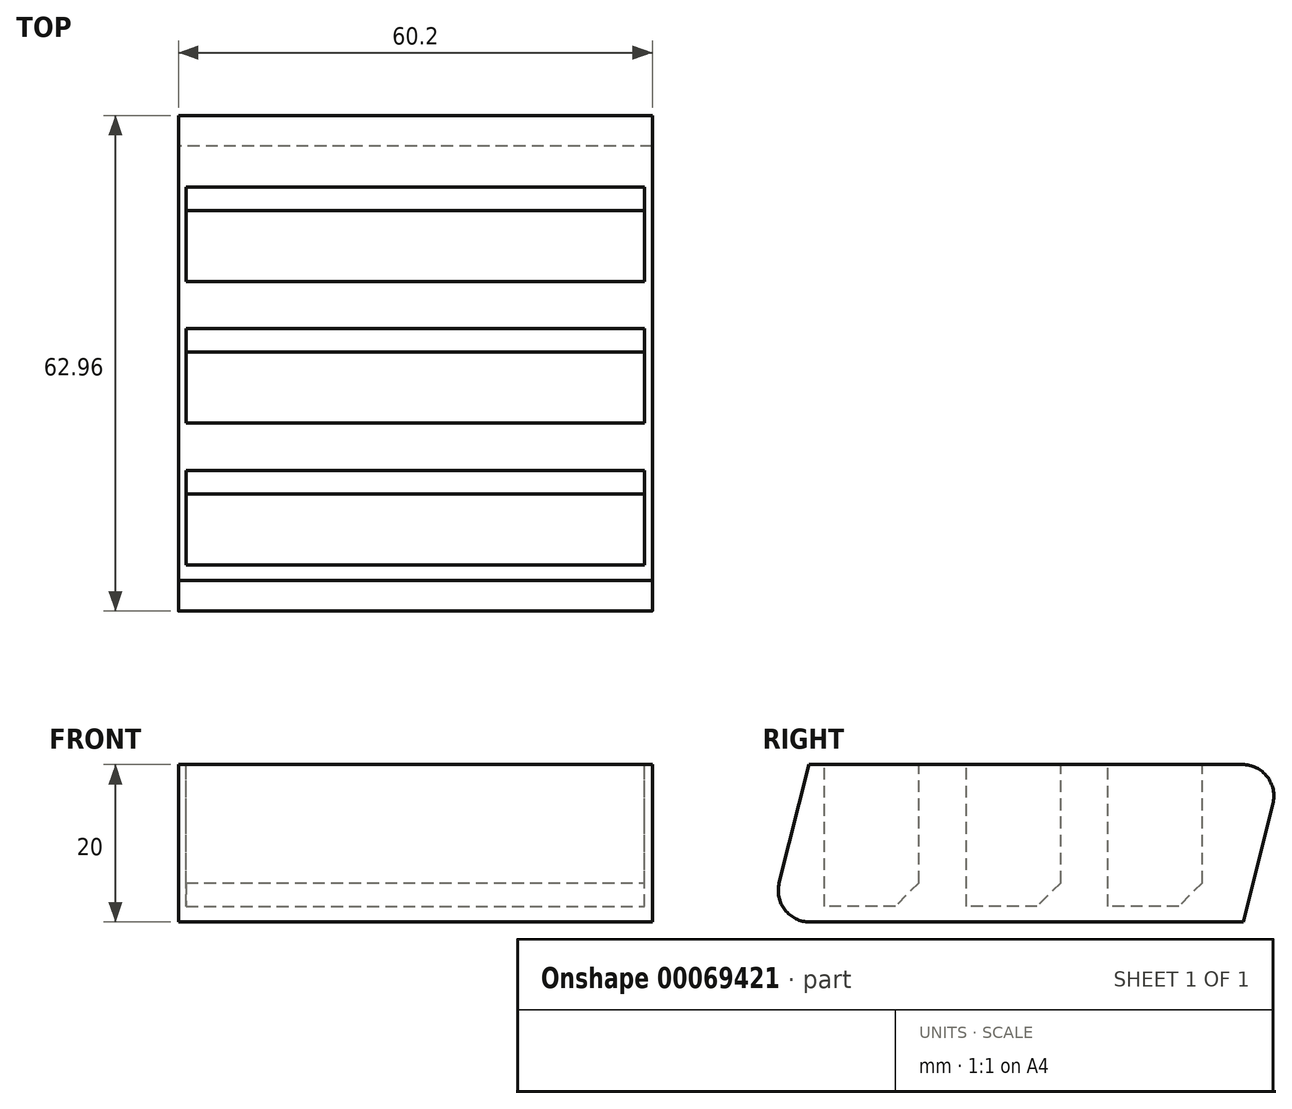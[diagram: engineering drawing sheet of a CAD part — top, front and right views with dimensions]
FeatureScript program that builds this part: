
annotation { "Feature Type Name" : "Feature", "Feature Type Description" : "" }
export const myFeature = defineFeature(function(context is Context, id is Id, definition is map)
    precondition{}
    {
        {
            var Q0;
            Q0=qCreatedBy(makeId("Top.planeOp"),FACE);
            var sketch = newSketch(context, id + "F0", { "sketchPlane" : qUnion([Q0])});
            skLineSegment(sketch, "E0.rect.bottom", {"start": v(30.1, -30.1) * mm, "end": v(-30.1, -30.1) * mm});
            skLineSegment(sketch, "E0.rect.top", {"start": v(30.1, 30.1) * mm, "end": v(-30.1, 30.1) * mm});
            skLineSegment(sketch, "E0.rect.left", {"start": v(30.1, -30.1) * mm, "end": v(30.1, 30.1) * mm});
            skLineSegment(sketch, "E0.rect.right", {"start": v(-30.1, -30.1) * mm, "end": v(-30.1, 30.1) * mm});
            skPoint(sketch, "E0.rect.middle", {"position": v(0, 0) * mm});
            skSolve(sketch);
        }
        {
            var Q0;
            Q0=makeQuery(id+"F0.imprint","IMPRINT",FACE,{"disambiguationData":[TD([[makeQuery(id+"F0.imprint","IMPRINT",EDGE,{"derivedFrom":sQuery(id+"F0.wireOp",EDGE,"E0.rect.bottom")}),-1.0]])]});
            cPlane(context, id + "F1", {"entities" : qUnion([Q0]), "cplaneType" : CPlaneType.OFFSET, "offset" : 20 * mm, "width" : 150 * mm, "height" : 150 * mm});
        }
        {
            var Q0;
            Q0=qCreatedBy(id+"F1.planeOp",FACE);
            var sketch = newSketch(context, id + "F2", { "sketchPlane" : qUnion([Q0])});
            skLineSegment(sketch, "E1.0.0", {"start": v(-30.1, -30.1) * mm, "end": v(30.1, -30.1) * mm, "construction": true});
            skLineSegment(sketch, "E1.0.1", {"start": v(30.1, -30.1) * mm, "end": v(30.1, 30.1) * mm, "construction": true});
            skLineSegment(sketch, "E1.0.2", {"start": v(30.1, 30.1) * mm, "end": v(-30.1, 30.1) * mm, "construction": true});
            skLineSegment(sketch, "E1.0.3", {"start": v(-30.1, 30.1) * mm, "end": v(-30.1, -30.1) * mm, "construction": true});
            skLineSegment(sketch, "E2", {"start": v(0, 0) * mm, "end": v(0, 5) * mm, "construction": true});
            skLineSegment(sketch, "E3.rect.bottom", {"start": v(30.1, 35.1) * mm, "end": v(-30.1, 35.1) * mm});
            skLineSegment(sketch, "E3.rect.top", {"start": v(30.1, -25.1) * mm, "end": v(-30.1, -25.1) * mm});
            skLineSegment(sketch, "E3.rect.left", {"start": v(30.1, 35.1) * mm, "end": v(30.1, -25.1) * mm});
            skLineSegment(sketch, "E3.rect.right", {"start": v(-30.1, 35.1) * mm, "end": v(-30.1, -25.1) * mm});
            skPoint(sketch, "E3.rect.middle", {"position": v(0, 5) * mm});
            skSolve(sketch);
        }
        {
            var Q0;
            Q0=makeQuery(id+"F0.imprint","IMPRINT",FACE,{"disambiguationData":[TD([[makeQuery(id+"F0.imprint","IMPRINT",EDGE,{"derivedFrom":sQuery(id+"F0.wireOp",EDGE,"E0.rect.bottom")}),-1.0]])]});
            var Q1;
            Q1=makeQuery(id+"F2.imprint","IMPRINT",FACE,{"disambiguationData":[TD([[makeQuery(id+"F2.imprint","IMPRINT",EDGE,{"derivedFrom":sQuery(id+"F2.wireOp",EDGE,"E3.rect.bottom")}),1.0]])]});
            loft(context, id + "F3", {"sheetProfilesArray" : [{ "sheetProfileEntities" : qUnion([Q0]) }, { "sheetProfileEntities" : qUnion([Q1]) }]});
        }
        {
            var Q0;
            Q0=makeQuery(id+"F3.opLoft","CAP_FACE",FACE,{"disambiguationData":[OSD([makeQuery(id+"F2.imprint","IMPRINT",FACE,{"disambiguationData":[TD([[makeQuery(id+"F2.imprint","IMPRINT",EDGE,{"derivedFrom":sQuery(id+"F2.wireOp",EDGE,"E3.rect.bottom")}),1.0]])]})])],"isStart":true});
            var sketch = newSketch(context, id + "F4", { "sketchPlane" : qUnion([Q0])});
            skLineSegment(sketch, "E4", {"start": v(0, -25.1) * mm, "end": v(0, -17.1) * mm, "construction": true});
            skLineSegment(sketch, "E5.rect.bottom", {"start": v(-29.1, -11.1) * mm, "end": v(29.1, -11.1) * mm});
            skLineSegment(sketch, "E5.rect.top", {"start": v(-29.1, -23.1) * mm, "end": v(29.1, -23.1) * mm});
            skLineSegment(sketch, "E5.rect.left", {"start": v(-29.1, -11.1) * mm, "end": v(-29.1, -23.1) * mm});
            skLineSegment(sketch, "E5.rect.right", {"start": v(29.1, -11.1) * mm, "end": v(29.1, -23.1) * mm});
            skPoint(sketch, "E5.rect.middle", {"position": v(0, -17.1) * mm});
            skLineSegment(sketch, "E6", {"start": v(29.1, -23.1) * mm, "end": v(30.1, -23.1) * mm, "construction": true});
            skLineSegment(sketch, "E7", {"start": v(30.1, -23.1) * mm, "end": v(29.1, -23.1) * mm, "construction": true});
            skLineSegment(sketch, "E8", {"start": v(29.1, -23.1) * mm, "end": v(29.1, -25.1) * mm, "construction": true});
            skLineSegment(sketch, "E9.0.1.0", {"start": v(-29.1, 6.9) * mm, "end": v(29.1, 6.9) * mm});
            skLineSegment(sketch, "E9.0.1.1", {"start": v(-29.1, 6.9) * mm, "end": v(-29.1, -5.1) * mm});
            skLineSegment(sketch, "E9.0.1.2", {"start": v(-29.1, -5.1) * mm, "end": v(29.1, -5.1) * mm});
            skLineSegment(sketch, "E9.0.1.3", {"start": v(29.1, 6.9) * mm, "end": v(29.1, -5.1) * mm});
            skLineSegment(sketch, "E9.0.2.0", {"start": v(-29.1, 24.9) * mm, "end": v(29.1, 24.9) * mm});
            skLineSegment(sketch, "E9.0.2.1", {"start": v(-29.1, 24.9) * mm, "end": v(-29.1, 12.9) * mm});
            skLineSegment(sketch, "E9.0.2.2", {"start": v(-29.1, 12.9) * mm, "end": v(29.1, 12.9) * mm});
            skLineSegment(sketch, "E9.0.2.3", {"start": v(29.1, 24.9) * mm, "end": v(29.1, 12.9) * mm});
            skLineSegment(sketch, "E9.direction1", {"start": v(-29.1, -11.1) * mm, "end": v(-3.95, -11.1) * mm, "construction": true});
            skLineSegment(sketch, "E9.direction2", {"start": v(-29.1, -11.1) * mm, "end": v(-29.1, 6.9) * mm, "construction": true});
            skSolve(sketch);
        }
        {
            var Q0;
            Q0 = qSketchRegion(id + "F4", true);
            extrude(context, id + "F5", {"entities" : qUnion([Q0]), "operationType" : NewBodyOperationType.REMOVE, "oppositeDirection" : true, "depth" : 18 * mm});
        }
        {
            var Q0;
            Q0=makeQuery(id+"F3.opLoft","MID_CAP_EDGE",EDGE,{"disambiguationData":[OSD([sQuery(id+"F0.wireOp",EDGE,"E0.rect.bottom"),sQuery(id+"F0.wireOp",EDGE,"E0.rect.left"),sQuery(id+"F0.wireOp",EDGE,"E0.rect.right")])],"capPos":0.0});
            var Q1;
            Q1=makeQuery(id+"F3.opLoft","MID_CAP_EDGE",EDGE,{"disambiguationData":[OSD([sQuery(id+"F2.wireOp",EDGE,"E3.rect.bottom"),sQuery(id+"F2.wireOp",EDGE,"E3.rect.left"),sQuery(id+"F2.wireOp",EDGE,"E3.rect.right")])],"capPos":1.0});
            var Q2;
            Q2=makeQuery(id+"F5.boolean.opBoolean","COPY",EDGE,{"derivedFrom":makeQuery(id+"F5.opExtrude","CAP_EDGE",EDGE,{"disambiguationData":[OSD([sQuery(id+"F4.wireOp",EDGE,"E5.rect.bottom")])],"isStart":true})});
            var Q3;
            Q3=makeQuery(id+"F5.boolean.opBoolean","COPY",EDGE,{"derivedFrom":makeQuery(id+"F5.opExtrude","CAP_EDGE",EDGE,{"disambiguationData":[OSD([sQuery(id+"F4.wireOp",EDGE,"E9.0.1.0")])],"isStart":true})});
            var Q4;
            Q4=makeQuery(id+"F5.boolean.opBoolean","COPY",EDGE,{"derivedFrom":makeQuery(id+"F5.opExtrude","CAP_EDGE",EDGE,{"disambiguationData":[OSD([sQuery(id+"F4.wireOp",EDGE,"E9.0.2.0")])],"isStart":true})});
            fillet(context, id + "F6", {"entities" : qUnion([Q0, Q1, Q2, Q3, Q4]), "radius" : 4 * mm, "tangentPropagation" : true, "allowEdgeOverflow" : false});
        }
        {
            var Q0;
            Q0=makeQuery(id+"F5.boolean.opBoolean","COPY",EDGE,{"derivedFrom":makeQuery(id+"F5.opExtrude","CAP_EDGE",EDGE,{"disambiguationData":[OSD([sQuery(id+"F4.wireOp",EDGE,"E9.0.2.0")])],"isStart":false})});
            var Q1;
            Q1=makeQuery(id+"F5.boolean.opBoolean","COPY",EDGE,{"derivedFrom":makeQuery(id+"F5.opExtrude","CAP_EDGE",EDGE,{"disambiguationData":[OSD([sQuery(id+"F4.wireOp",EDGE,"E9.0.1.0")])],"isStart":false})});
            var Q2;
            Q2=makeQuery(id+"F5.boolean.opBoolean","COPY",EDGE,{"derivedFrom":makeQuery(id+"F5.opExtrude","CAP_EDGE",EDGE,{"disambiguationData":[OSD([sQuery(id+"F4.wireOp",EDGE,"E5.rect.bottom")])],"isStart":false})});
            chamfer(context, id + "F7", {"entities" : qUnion([Q0, Q1, Q2]), "width" : 3 * mm, "tangentPropagation" : true});
        }
    });
